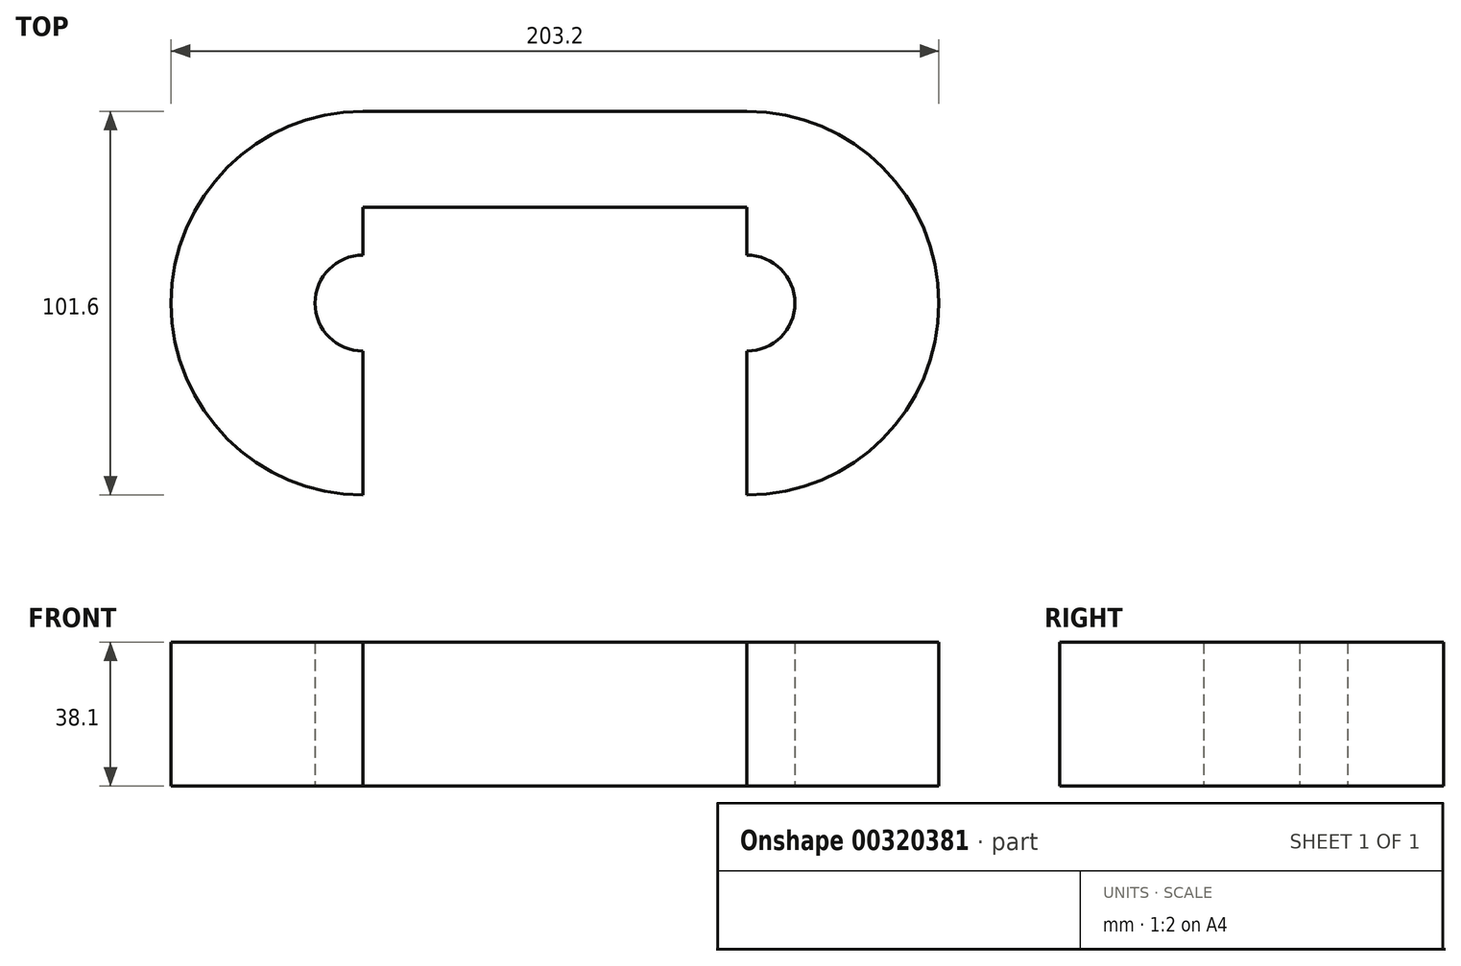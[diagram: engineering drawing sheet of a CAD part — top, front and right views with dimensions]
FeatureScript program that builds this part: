
annotation { "Feature Type Name" : "Feature", "Feature Type Description" : "" }
export const myFeature = defineFeature(function(context is Context, id is Id, definition is map)
    precondition{}
    {
        {
            var Q0;
            Q0=qCreatedBy(makeId("Top.planeOp"),FACE);
            var sketch = newSketch(context, id + "F0", { "sketchPlane" : qUnion([Q0])});
            skCircle(sketch, "E0", {"center": v(0, 0) * mm, "radius": 12.7 * mm});
            skCircle(sketch, "E1", {"center": v(101.6, 0) * mm, "radius": 12.7 * mm});
            skLineSegment(sketch, "E2", {"start": v(0, -50.8) * mm, "end": v(101.6, -50.8) * mm});
            skLineSegment(sketch, "E3", {"start": v(0, 50.8) * mm, "end": v(101.6, 50.8) * mm});
            skArc(sketch, "E4", {"start": v(101.6, -50.8) * mm, "mid": v(152.4, 0) * mm, "end": v(101.6, 50.8) * mm});
            skArc(sketch, "E5", {"start": v(0, 50.8) * mm, "mid": v(-50.8, 0) * mm, "end": v(0, -50.8) * mm});
            skLineSegment(sketch, "E6", {"start": v(-50.8, 0) * mm, "end": v(152.4, 0) * mm, "construction": true});
            skSolve(sketch);
        }
        {
            var Q0;
            Q0=makeQuery(id+"F0.imprint","IMPRINT",FACE,{"disambiguationData":[TD([[makeQuery(id+"F0.imprint","IMPRINT",EDGE,{"derivedFrom":sQuery(id+"F0.wireOp",EDGE,"E0")}),-1.0]])]});
            extrude(context, id + "F1", {"entities" : qUnion([Q0]), "depth" : 12.7 * mm});
        }
        {
            var Q0;
            Q0=makeQuery(id+"F1.opExtrude","SWEPT_FACE",FACE,{"disambiguationData":[OSD([sQuery(id+"F0.wireOp",EDGE,"E2")])]});
            extrude(context, id + "F2", {"entities" : qUnion([Q0]), "operationType" : NewBodyOperationType.REMOVE, "oppositeDirection" : true, "depth" : 76.2 * mm});
        }
        {
            var Q0;
            Q0=makeQuery(id+"F1.opExtrude","CAP_FACE",FACE,{"disambiguationData":[OSD([sQuery(id+"F0.wireOp",EDGE,"E0"),sQuery(id+"F0.wireOp",EDGE,"E1"),sQuery(id+"F0.wireOp",EDGE,"E2"),sQuery(id+"F0.wireOp",EDGE,"E3"),sQuery(id+"F0.wireOp",EDGE,"E4"),sQuery(id+"F0.wireOp",EDGE,"E5")])],"isStart":false});
            extrude(context, id + "F3", {"entities" : qUnion([Q0]), "operationType" : NewBodyOperationType.ADD, "depth" : 25.4 * mm});
        }
    });
